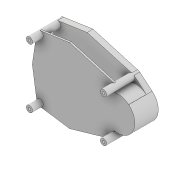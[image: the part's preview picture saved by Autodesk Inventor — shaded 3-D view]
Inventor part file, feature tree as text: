
AUTODESK INVENTOR PART (.ipt)
format: ipt  version: 2020 (Build 240168000, 168)  size: 232,448 bytes
history: native  units: mm
features: extrude x4, sketch x4, other x1
ambient origin geometry x8: Origin, YZ Plane, XZ Plane, XY Plane, X Axis, Y Axis, Z Axis, Center Point
bodies: Body1 (feature_tree)
feature tree (9):
  other  "솔리드1"
  extrude  "돌출1"  Depth=35.14mm
  extrude  "돌출2"  Depth=96.74mm
  extrude  "돌출3"  Depth=70.28mm
  extrude  "돌출4"  Depth=27.87mm
  sketch  "스케치1"
  sketch  "스케치2"
  sketch  "스케치3"
  sketch  "스케치4"
